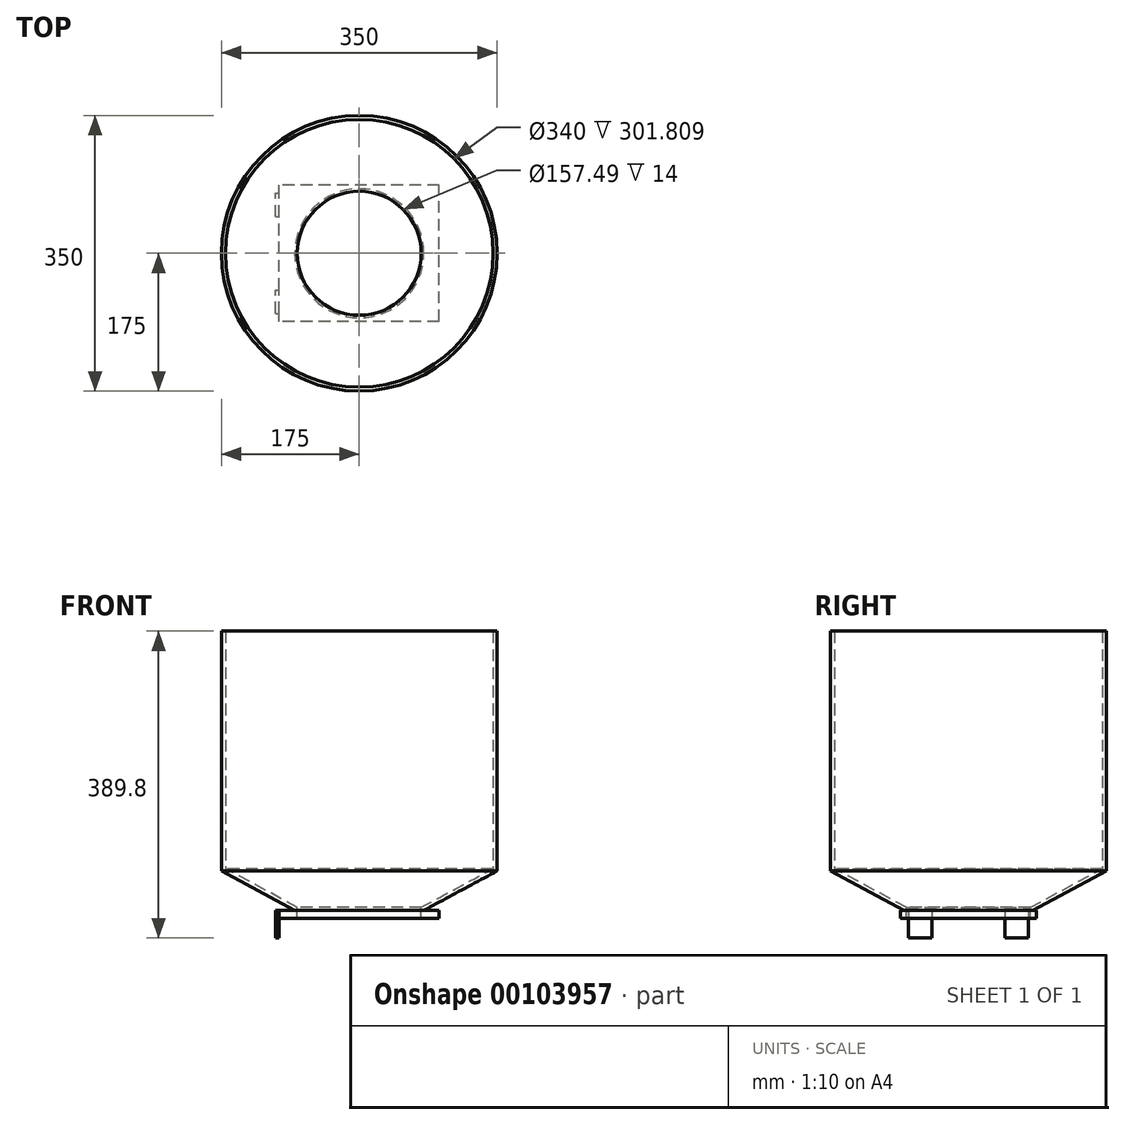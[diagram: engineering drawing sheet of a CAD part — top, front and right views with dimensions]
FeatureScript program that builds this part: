
annotation { "Feature Type Name" : "Feature", "Feature Type Description" : "" }
export const myFeature = defineFeature(function(context is Context, id is Id, definition is map)
    precondition{}
    {
        {
            var Q0;
            Q0=qCreatedBy(makeId("Top.planeOp"),FACE);
            var sketch = newSketch(context, id + "F0", { "sketchPlane" : qUnion([Q0])});
            skLineSegment(sketch, "E0.bottom", {"start": v(101.6, -86.4) * mm, "end": v(-101.6, -86.4) * mm});
            skLineSegment(sketch, "E0.top", {"start": v(101.6, 86.4) * mm, "end": v(-101.6, 86.4) * mm});
            skLineSegment(sketch, "E0.left", {"start": v(101.6, -86.4) * mm, "end": v(101.6, 86.4) * mm});
            skLineSegment(sketch, "E0.right", {"start": v(-101.6, -86.4) * mm, "end": v(-101.6, 86.4) * mm});
            skPoint(sketch, "E0.middle", {"position": v(0, 0) * mm});
            skSolve(sketch);
        }
        {
            var Q0;
            Q0=makeQuery(id+"F0.imprint","IMPRINT",FACE,{"disambiguationData":[TD([[makeQuery(id+"F0.imprint","IMPRINT",EDGE,{"derivedFrom":sQuery(id+"F0.wireOp",EDGE,"E0.bottom")}),-1.0]])]});
            extrude(context, id + "F1", {"entities" : qUnion([Q0]), "depth" : 10 * mm});
        }
        {
            var Q0;
            Q0=makeQuery(id+"F1.opExtrude","CAP_FACE",FACE,{"disambiguationData":[OSD([sQuery(id+"F0.wireOp",EDGE,"E0.bottom"),sQuery(id+"F0.wireOp",EDGE,"E0.top"),sQuery(id+"F0.wireOp",EDGE,"E0.left"),sQuery(id+"F0.wireOp",EDGE,"E0.right")])],"isStart":false});
            var sketch = newSketch(context, id + "F2", { "sketchPlane" : qUnion([Q0])});
            skCircle(sketch, "E1", {"center": v(0, 0) * mm, "radius": 77.5 * mm});
            skSolve(sketch);
        }
        {
            var Q0;
            Q0 = qSketchRegion(id + "F2", true);
            extrude(context, id + "F3", {"entities" : qUnion([Q0]), "operationType" : NewBodyOperationType.REMOVE, "endBound" : BoundingType.THROUGH_ALL, "oppositeDirection" : true, "depth" : 25 * mm});
        }
        {
            var Q0;
            Q0=makeQuery(id+"F1.opExtrude","CAP_FACE",FACE,{"disambiguationData":[OSD([sQuery(id+"F0.wireOp",EDGE,"E0.bottom"),sQuery(id+"F0.wireOp",EDGE,"E0.top"),sQuery(id+"F0.wireOp",EDGE,"E0.left"),sQuery(id+"F0.wireOp",EDGE,"E0.right")])],"isStart":false});
            cPlane(context, id + "F4", {"entities" : qUnion([Q0]), "cplaneType" : CPlaneType.OFFSET, "offset" : 50 * mm, "width" : 150 * mm, "height" : 150 * mm});
        }
        {
            var Q0;
            Q0=qCreatedBy(id+"F4.planeOp",FACE);
            var sketch = newSketch(context, id + "F5", { "sketchPlane" : qUnion([Q0])});
            skCircle(sketch, "E2", {"center": v(0, 0) * mm, "radius": 175 * mm});
            skPoint(sketch, "E3", {"position": v(0, 175) * mm});
            skSolve(sketch);
        }
        {
            var Q0;
            Q0=makeQuery(id+"F1.opExtrude","CAP_FACE",FACE,{"disambiguationData":[OSD([sQuery(id+"F0.wireOp",EDGE,"E0.bottom"),sQuery(id+"F0.wireOp",EDGE,"E0.top"),sQuery(id+"F0.wireOp",EDGE,"E0.left"),sQuery(id+"F0.wireOp",EDGE,"E0.right")])],"isStart":false});
            cPlane(context, id + "F6", {"entities" : qUnion([Q0]), "cplaneType" : CPlaneType.OFFSET, "offset" : 1 * mm, "oppositeDirection" : true, "width" : 150 * mm, "height" : 150 * mm});
        }
        {
            var Q0;
            Q0=qCreatedBy(id+"F6.planeOp",FACE);
            var sketch = newSketch(context, id + "F7", { "sketchPlane" : qUnion([Q0])});
            skCircle(sketch, "E4", {"center": v(0, 0) * mm, "radius": 80 * mm});
            skSolve(sketch);
        }
        {
            var Q0;
            Q0 = qSketchRegion(id + "F5", true);
            var Q1;
            Q1 = qSketchRegion(id + "F7", true);
            loft(context, id + "F8", {"operationType" : NewBodyOperationType.ADD, "sheetProfilesArray" : [{ "sheetProfileEntities" : qUnion([Q0]) }, { "sheetProfileEntities" : qUnion([Q1]) }]});
        }
        {
            var Q0;
            Q0=makeQuery(id+"F8.opLoft","CAP_FACE",FACE,{"disambiguationData":[OSD([makeQuery(id+"F5.imprint","IMPRINT",FACE,{"disambiguationData":[TD([[makeQuery(id+"F5.imprint","IMPRINT",EDGE,{"derivedFrom":sQuery(id+"F5.wireOp",EDGE,"E2")}),1.0]])]})])],"isStart":true});
            var sketch = newSketch(context, id + "F9", { "sketchPlane" : qUnion([Q0])});
            skCircle(sketch, "E5", {"center": v(0, 0) * mm, "radius": 175 * mm});
            skSolve(sketch);
        }
        {
            var Q0;
            Q0 = qSketchRegion(id + "F9", true);
            extrude(context, id + "F10", {"entities" : qUnion([Q0]), "operationType" : NewBodyOperationType.ADD, "depth" : 304.8 * mm});
        }
        {
            var Q0;
            Q0=makeQuery(id+"F10.opExtrude","CAP_FACE",FACE,{"disambiguationData":[OSD([sQuery(id+"F9.wireOp",EDGE,"E5")])],"isStart":false});
            shell(context, id + "F11", {"entities" : qUnion([Q0]), "thickness" : 5 * mm});
        }
        {
            var Q0;
            Q0=makeQuery(id+"F11.opShell","OFFSET_FACE",FACE,{"disambiguationData":[OSD([makeQuery(id+"F7.imprint","IMPRINT",FACE,{"disambiguationData":[TD([[makeQuery(id+"F7.imprint","IMPRINT",EDGE,{"derivedFrom":sQuery(id+"F7.wireOp",EDGE,"E4")}),1.0]])]})])]});
            var sketch = newSketch(context, id + "F12", { "sketchPlane" : qUnion([Q0])});
            skCircle(sketch, "E6", {"center": v(0, 0) * mm, "radius": 78.74 * mm});
            skSolve(sketch);
        }
        {
            var Q0;
            Q0 = qSketchRegion(id + "F12", true);
            extrude(context, id + "F13", {"entities" : qUnion([Q0]), "operationType" : NewBodyOperationType.REMOVE, "endBound" : BoundingType.THROUGH_ALL, "oppositeDirection" : true, "depth" : 25 * mm});
        }
        {
            var Q0;
            Q0=makeQuery(id+"F1.opExtrude","SWEPT_FACE",FACE,{"disambiguationData":[OSD([sQuery(id+"F0.wireOp",EDGE,"E0.right")])]});
            var sketch = newSketch(context, id + "F14", { "sketchPlane" : qUnion([Q0])});
            skLineSegment(sketch, "E7.bottom", {"start": v(-86.4, 10) * mm, "end": v(-76.4, 10) * mm, "construction": true});
            skLineSegment(sketch, "E7.top", {"start": v(-86.4, -25) * mm, "end": v(-76.4, -25) * mm, "construction": true});
            skLineSegment(sketch, "E7.left", {"start": v(-86.4, 10) * mm, "end": v(-86.4, -25) * mm, "construction": true});
            skLineSegment(sketch, "E7.right", {"start": v(-76.4, 10) * mm, "end": v(-76.4, -25) * mm, "construction": true});
            skLineSegment(sketch, "E8.bottom", {"start": v(-46.4, 10) * mm, "end": v(-36.4, 10) * mm, "construction": true});
            skLineSegment(sketch, "E8.top", {"start": v(-46.4, -25) * mm, "end": v(-36.4, -25) * mm, "construction": true});
            skLineSegment(sketch, "E8.left", {"start": v(-46.4, 10) * mm, "end": v(-46.4, -25) * mm, "construction": true});
            skLineSegment(sketch, "E8.right", {"start": v(-36.4, 10) * mm, "end": v(-36.4, -25) * mm, "construction": true});
            skLineSegment(sketch, "E9.bottom", {"start": v(36.4, 10) * mm, "end": v(46.4, 10) * mm, "construction": true});
            skLineSegment(sketch, "E9.top", {"start": v(36.4, -25) * mm, "end": v(46.4, -25) * mm, "construction": true});
            skLineSegment(sketch, "E9.left", {"start": v(36.4, 10) * mm, "end": v(36.4, -25) * mm, "construction": true});
            skLineSegment(sketch, "E9.right", {"start": v(46.4, 10) * mm, "end": v(46.4, -25) * mm, "construction": true});
            skLineSegment(sketch, "E10.bottom", {"start": v(76.4, 10) * mm, "end": v(86.4, 10) * mm, "construction": true});
            skLineSegment(sketch, "E10.top", {"start": v(76.4, -25) * mm, "end": v(86.4, -25) * mm, "construction": true});
            skLineSegment(sketch, "E10.left", {"start": v(76.4, 10) * mm, "end": v(76.4, -25) * mm, "construction": true});
            skLineSegment(sketch, "E10.right", {"start": v(86.4, 10) * mm, "end": v(86.4, -25) * mm, "construction": true});
            skLineSegment(sketch, "E11.bottom", {"start": v(-76.4, 10) * mm, "end": v(-46.4, 10) * mm});
            skLineSegment(sketch, "E11.top", {"start": v(-76.4, -25) * mm, "end": v(-46.4, -25) * mm});
            skLineSegment(sketch, "E11.left", {"start": v(-76.4, 10) * mm, "end": v(-76.4, -25) * mm});
            skLineSegment(sketch, "E11.right", {"start": v(-46.4, 10) * mm, "end": v(-46.4, -25) * mm});
            skLineSegment(sketch, "E12.bottom", {"start": v(46.4, 10) * mm, "end": v(76.4, 10) * mm});
            skLineSegment(sketch, "E12.top", {"start": v(46.4, -25) * mm, "end": v(76.4, -25) * mm});
            skLineSegment(sketch, "E12.left", {"start": v(46.4, 10) * mm, "end": v(46.4, -25) * mm});
            skLineSegment(sketch, "E12.right", {"start": v(76.4, 10) * mm, "end": v(76.4, -25) * mm});
            skSolve(sketch);
        }
        {
            var Q0;
            Q0 = qSketchRegion(id + "F14", true);
            extrude(context, id + "F15", {"entities" : qUnion([Q0]), "operationType" : NewBodyOperationType.ADD, "depth" : 5 * mm});
        }
        {
            var Q0;
            Q0=makeQuery(id+"F15.opExtrude","CAP_FACE",FACE,{"disambiguationData":[OSD([sQuery(id+"F14.wireOp",EDGE,"E12.bottom"),sQuery(id+"F14.wireOp",EDGE,"E12.top"),sQuery(id+"F14.wireOp",EDGE,"E12.left"),sQuery(id+"F14.wireOp",EDGE,"E12.right")])],"isStart":true});
            cPlane(context, id + "F16", {"entities" : qUnion([Q0]), "cplaneType" : CPlaneType.OFFSET, "offset" : 101.6 * mm, "width" : 150 * mm, "height" : 150 * mm});
        }
    });
